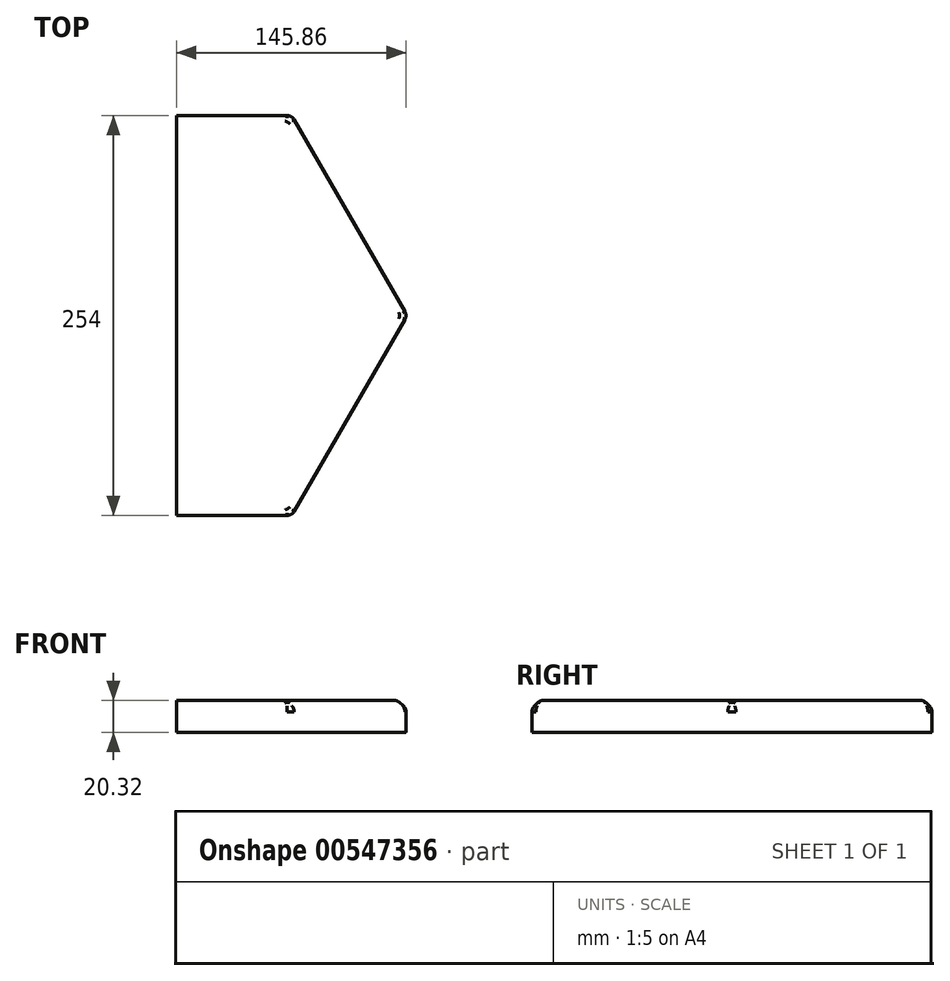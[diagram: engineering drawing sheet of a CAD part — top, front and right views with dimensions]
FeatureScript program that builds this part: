
annotation { "Feature Type Name" : "Feature", "Feature Type Description" : "" }
export const myFeature = defineFeature(function(context is Context, id is Id, definition is map)
    precondition{}
    {
        {
            var Q0;
            Q0=qCreatedBy(makeId("Top.planeOp"),FACE);
            var sketch = newSketch(context, id + "F0", { "sketchPlane" : qUnion([Q0])});
            skCircle(sketch, "E0.cCircle", {"center": v(0, 0) * mm, "radius": 127 * mm, "construction": true});
            skLineSegment(sketch, "E0.0", {"start": v(73.32, 127) * mm, "end": v(146.65, 0) * mm});
            skLineSegment(sketch, "E0.1", {"start": v(146.65, 0) * mm, "end": v(73.32, -127) * mm});
            skLineSegment(sketch, "E0.2", {"start": v(73.32, -127) * mm, "end": v(-73.32, -127) * mm});
            skLineSegment(sketch, "E0.3", {"start": v(-73.32, -127) * mm, "end": v(-146.65, 0) * mm});
            skLineSegment(sketch, "E0.4", {"start": v(-146.65, 0) * mm, "end": v(-73.32, 127) * mm});
            skLineSegment(sketch, "E0.5", {"start": v(-73.32, 127) * mm, "end": v(73.32, 127) * mm});
            skPoint(sketch, "E0.0.midPoint", {"position": v(109.99, 63.5) * mm});
            skSolve(sketch);
        }
        {
            var Q0;
            Q0 = qSketchRegion(id + "F0", true);
            extrude(context, id + "F1", {"entities" : qUnion([Q0]), "depth" : 20.32 * mm, "offsetDistance" : 25.4 * mm});
        }
        {
            var Q0;
            Q0=makeQuery(id+"F1.opExtrude","CAP_EDGE",EDGE,{"disambiguationData":[OSD([sQuery(id+"F0.wireOp",EDGE,"E0.3")])],"isStart":false});
            var Q1;
            Q1=makeQuery(id+"F1.opExtrude","CAP_EDGE",EDGE,{"disambiguationData":[OSD([sQuery(id+"F0.wireOp",EDGE,"E0.2")])],"isStart":false});
            var Q2;
            Q2=makeQuery(id+"F1.opExtrude","CAP_EDGE",EDGE,{"disambiguationData":[OSD([sQuery(id+"F0.wireOp",EDGE,"E0.1")])],"isStart":false});
            var Q3;
            Q3=makeQuery(id+"F1.opExtrude","CAP_EDGE",EDGE,{"disambiguationData":[OSD([sQuery(id+"F0.wireOp",EDGE,"E0.0")])],"isStart":false});
            var Q4;
            Q4=makeQuery(id+"F1.opExtrude","CAP_EDGE",EDGE,{"disambiguationData":[OSD([sQuery(id+"F0.wireOp",EDGE,"E0.5")])],"isStart":false});
            var Q5;
            Q5=makeQuery(id+"F1.opExtrude","CAP_EDGE",EDGE,{"disambiguationData":[OSD([sQuery(id+"F0.wireOp",EDGE,"E0.4")])],"isStart":false});
            chamfer(context, id + "F2", {"entities" : qUnion([Q0, Q1, Q2, Q3, Q4, Q5]), "width" : 5.08 * mm, "tangentPropagation" : true});
        }
        {
            var Q0;
            Q0=makeQuery(id+"F1.opExtrude","CAP_FACE",FACE,{"disambiguationData":[OSD([sQuery(id+"F0.wireOp",EDGE,"E0.0"),sQuery(id+"F0.wireOp",EDGE,"E0.1"),sQuery(id+"F0.wireOp",EDGE,"E0.2"),sQuery(id+"F0.wireOp",EDGE,"E0.3"),sQuery(id+"F0.wireOp",EDGE,"E0.4"),sQuery(id+"F0.wireOp",EDGE,"E0.5")])],"isStart":false});
            var sketch = newSketch(context, id + "F3", { "sketchPlane" : qUnion([Q0])});
            skLineSegment(sketch, "E1.bottom", {"start": v(0, 161.52) * mm, "end": v(-159.86, 161.52) * mm});
            skLineSegment(sketch, "E1.top", {"start": v(0, -144.8) * mm, "end": v(-159.86, -144.8) * mm});
            skLineSegment(sketch, "E1.left", {"start": v(0, 161.52) * mm, "end": v(0, -144.8) * mm});
            skLineSegment(sketch, "E1.right", {"start": v(-159.86, 161.52) * mm, "end": v(-159.86, -144.8) * mm});
            skSolve(sketch);
        }
        {
            var Q0;
            {var subQ9=sQuery(id+"F3.wireOp",EDGE,"E1.bottom");Q0=makeQuery(id+"F3.imprint","IMPRINT",FACE,{"disambiguationData":[TD([[makeQuery(id+"F3.imprint","IMPRINT",EDGE,{"derivedFrom":subQ9}),1.0]])]});}
            var Q1;
            {var subQ0=sQuery(id+"F0.wireOp",EDGE,"E0.5");var subQ1=sQuery(id+"F0.wireOp",EDGE,"E0.4");var subQ2=sQuery(id+"F0.wireOp",EDGE,"E0.3");var subQ3=sQuery(id+"F0.wireOp",EDGE,"E0.2");var subQ4=makeQuery(id+"F1.opExtrude","CAP_FACE",FACE,{"disambiguationData":[OSD([sQuery(id+"F0.wireOp",EDGE,"E0.0"),sQuery(id+"F0.wireOp",EDGE,"E0.1"),subQ3,subQ2,subQ1,subQ0])],"isStart":false});var subQ5=makeQuery(id+"F2.opChamfer","BLEND_EDGE",EDGE,{"blendedFrom":[makeQuery(id+"F1.opExtrude","CAP_EDGE",EDGE,{"disambiguationData":[OSD([subQ2])],"isStart":false}),subQ4],"blendedInto":[subQ4]});Q1=makeQuery(id+"F3.imprint","IMPRINT",FACE,{"disambiguationData":[TD([[makeQuery(id+"F3.imprint","IMPRINT",EDGE,{"derivedFrom":subQ5}),1.0]])]});}
            extrude(context, id + "F4", {"entities" : qUnion([Q0, Q1]), "operationType" : NewBodyOperationType.REMOVE, "endBound" : BoundingType.THROUGH_ALL, "oppositeDirection" : true, "depth" : 25.4 * mm, "offsetDistance" : 25.4 * mm});
        }
        {
            var Q0;
            {var subQ0=sQuery(id+"F0.wireOp",EDGE,"E0.2");Q0=makeQuery(id+"F2.opChamfer","BLEND_EDGE",EDGE,{"blendedFrom":[makeQuery(id+"F1.opExtrude","CAP_EDGE",EDGE,{"disambiguationData":[OSD([subQ0])],"isStart":false}),makeQuery(id+"F1.opExtrude","CAP_FACE",FACE,{"disambiguationData":[OSD([sQuery(id+"F0.wireOp",EDGE,"E0.0"),sQuery(id+"F0.wireOp",EDGE,"E0.1"),subQ0,sQuery(id+"F0.wireOp",EDGE,"E0.3"),sQuery(id+"F0.wireOp",EDGE,"E0.4"),sQuery(id+"F0.wireOp",EDGE,"E0.5")])],"isStart":false})],"blendedInto":[makeQuery(id+"F1.opExtrude","CAP_FACE",FACE,{"disambiguationData":[OSD([sQuery(id+"F0.wireOp",EDGE,"E0.0"),sQuery(id+"F0.wireOp",EDGE,"E0.1"),subQ0,sQuery(id+"F0.wireOp",EDGE,"E0.3"),sQuery(id+"F0.wireOp",EDGE,"E0.4"),sQuery(id+"F0.wireOp",EDGE,"E0.5")])],"isStart":false})]});}
            var Q1;
            {var subQ0=sQuery(id+"F0.wireOp",EDGE,"E0.1");Q1=makeQuery(id+"F2.opChamfer","BLEND_EDGE",EDGE,{"blendedFrom":[makeQuery(id+"F1.opExtrude","CAP_EDGE",EDGE,{"disambiguationData":[OSD([subQ0])],"isStart":false}),makeQuery(id+"F1.opExtrude","CAP_FACE",FACE,{"disambiguationData":[OSD([sQuery(id+"F0.wireOp",EDGE,"E0.0"),subQ0,sQuery(id+"F0.wireOp",EDGE,"E0.2"),sQuery(id+"F0.wireOp",EDGE,"E0.3"),sQuery(id+"F0.wireOp",EDGE,"E0.4"),sQuery(id+"F0.wireOp",EDGE,"E0.5")])],"isStart":false})],"blendedInto":[makeQuery(id+"F1.opExtrude","CAP_FACE",FACE,{"disambiguationData":[OSD([sQuery(id+"F0.wireOp",EDGE,"E0.0"),subQ0,sQuery(id+"F0.wireOp",EDGE,"E0.2"),sQuery(id+"F0.wireOp",EDGE,"E0.3"),sQuery(id+"F0.wireOp",EDGE,"E0.4"),sQuery(id+"F0.wireOp",EDGE,"E0.5")])],"isStart":false})]});}
            var Q2;
            {var subQ0=sQuery(id+"F0.wireOp",EDGE,"E0.0");Q2=makeQuery(id+"F2.opChamfer","BLEND_EDGE",EDGE,{"blendedFrom":[makeQuery(id+"F1.opExtrude","CAP_EDGE",EDGE,{"disambiguationData":[OSD([subQ0])],"isStart":false}),makeQuery(id+"F1.opExtrude","CAP_FACE",FACE,{"disambiguationData":[OSD([subQ0,sQuery(id+"F0.wireOp",EDGE,"E0.1"),sQuery(id+"F0.wireOp",EDGE,"E0.2"),sQuery(id+"F0.wireOp",EDGE,"E0.3"),sQuery(id+"F0.wireOp",EDGE,"E0.4"),sQuery(id+"F0.wireOp",EDGE,"E0.5")])],"isStart":false})],"blendedInto":[makeQuery(id+"F1.opExtrude","CAP_FACE",FACE,{"disambiguationData":[OSD([subQ0,sQuery(id+"F0.wireOp",EDGE,"E0.1"),sQuery(id+"F0.wireOp",EDGE,"E0.2"),sQuery(id+"F0.wireOp",EDGE,"E0.3"),sQuery(id+"F0.wireOp",EDGE,"E0.4"),sQuery(id+"F0.wireOp",EDGE,"E0.5")])],"isStart":false})]});}
            var Q3;
            {var subQ0=sQuery(id+"F0.wireOp",EDGE,"E0.5");Q3=makeQuery(id+"F2.opChamfer","BLEND_EDGE",EDGE,{"blendedFrom":[makeQuery(id+"F1.opExtrude","CAP_EDGE",EDGE,{"disambiguationData":[OSD([subQ0])],"isStart":false}),makeQuery(id+"F1.opExtrude","CAP_FACE",FACE,{"disambiguationData":[OSD([sQuery(id+"F0.wireOp",EDGE,"E0.0"),sQuery(id+"F0.wireOp",EDGE,"E0.1"),sQuery(id+"F0.wireOp",EDGE,"E0.2"),sQuery(id+"F0.wireOp",EDGE,"E0.3"),sQuery(id+"F0.wireOp",EDGE,"E0.4"),subQ0])],"isStart":false})],"blendedInto":[makeQuery(id+"F1.opExtrude","CAP_FACE",FACE,{"disambiguationData":[OSD([sQuery(id+"F0.wireOp",EDGE,"E0.0"),sQuery(id+"F0.wireOp",EDGE,"E0.1"),sQuery(id+"F0.wireOp",EDGE,"E0.2"),sQuery(id+"F0.wireOp",EDGE,"E0.3"),sQuery(id+"F0.wireOp",EDGE,"E0.4"),subQ0])],"isStart":false})]});}
            var Q4;
            {var subQ0=sQuery(id+"F0.wireOp",EDGE,"E0.2");Q4=makeQuery(id+"F2.opChamfer","BLEND_EDGE",EDGE,{"blendedFrom":[makeQuery(id+"F1.opExtrude","CAP_EDGE",EDGE,{"disambiguationData":[OSD([subQ0])],"isStart":false}),makeQuery(id+"F1.opExtrude","SWEPT_FACE",FACE,{"disambiguationData":[OSD([subQ0])]})],"blendedInto":[makeQuery(id+"F1.opExtrude","SWEPT_FACE",FACE,{"disambiguationData":[OSD([subQ0])]})]});}
            var Q5;
            {var subQ0=sQuery(id+"F0.wireOp",EDGE,"E0.1");Q5=makeQuery(id+"F2.opChamfer","BLEND_EDGE",EDGE,{"blendedFrom":[makeQuery(id+"F1.opExtrude","CAP_EDGE",EDGE,{"disambiguationData":[OSD([subQ0])],"isStart":false}),makeQuery(id+"F1.opExtrude","SWEPT_FACE",FACE,{"disambiguationData":[OSD([subQ0])]})],"blendedInto":[makeQuery(id+"F1.opExtrude","SWEPT_FACE",FACE,{"disambiguationData":[OSD([subQ0])]})]});}
            var Q6;
            Q6=makeQuery(id+"F1.opExtrude","SWEPT_EDGE",EDGE,{"disambiguationData":[OSD([sQuery(id+"F0.wireOp",EDGE,"E0.1"),sQuery(id+"F0.wireOp",EDGE,"E0.2")])]});
            var Q7;
            Q7=makeQuery(id+"F2.opChamfer","BLEND_EDGE",EDGE,{"blendedFrom":[makeQuery(id+"F1.opExtrude","CAP_EDGE",EDGE,{"disambiguationData":[OSD([sQuery(id+"F0.wireOp",EDGE,"E0.1")])],"isStart":false}),makeQuery(id+"F1.opExtrude","CAP_EDGE",EDGE,{"disambiguationData":[OSD([sQuery(id+"F0.wireOp",EDGE,"E0.2")])],"isStart":false})],"blendedInto":[]});
            var Q8;
            Q8=makeQuery(id+"F2.opChamfer","BLEND_EDGE",EDGE,{"blendedFrom":[makeQuery(id+"F1.opExtrude","CAP_EDGE",EDGE,{"disambiguationData":[OSD([sQuery(id+"F0.wireOp",EDGE,"E0.0")])],"isStart":false}),makeQuery(id+"F1.opExtrude","CAP_EDGE",EDGE,{"disambiguationData":[OSD([sQuery(id+"F0.wireOp",EDGE,"E0.1")])],"isStart":false})],"blendedInto":[]});
            var Q9;
            Q9=makeQuery(id+"F1.opExtrude","SWEPT_EDGE",EDGE,{"disambiguationData":[OSD([sQuery(id+"F0.wireOp",EDGE,"E0.0"),sQuery(id+"F0.wireOp",EDGE,"E0.1")])]});
            var Q10;
            {var subQ0=sQuery(id+"F0.wireOp",EDGE,"E0.0");Q10=makeQuery(id+"F2.opChamfer","BLEND_EDGE",EDGE,{"blendedFrom":[makeQuery(id+"F1.opExtrude","CAP_EDGE",EDGE,{"disambiguationData":[OSD([subQ0])],"isStart":false}),makeQuery(id+"F1.opExtrude","SWEPT_FACE",FACE,{"disambiguationData":[OSD([subQ0])]})],"blendedInto":[makeQuery(id+"F1.opExtrude","SWEPT_FACE",FACE,{"disambiguationData":[OSD([subQ0])]})]});}
            var Q11;
            Q11=makeQuery(id+"F2.opChamfer","BLEND_EDGE",EDGE,{"blendedFrom":[makeQuery(id+"F1.opExtrude","CAP_EDGE",EDGE,{"disambiguationData":[OSD([sQuery(id+"F0.wireOp",EDGE,"E0.0")])],"isStart":false}),makeQuery(id+"F1.opExtrude","CAP_EDGE",EDGE,{"disambiguationData":[OSD([sQuery(id+"F0.wireOp",EDGE,"E0.5")])],"isStart":false})],"blendedInto":[]});
            var Q12;
            Q12=makeQuery(id+"F1.opExtrude","SWEPT_EDGE",EDGE,{"disambiguationData":[OSD([sQuery(id+"F0.wireOp",EDGE,"E0.0"),sQuery(id+"F0.wireOp",EDGE,"E0.5")])]});
            var Q13;
            {var subQ0=sQuery(id+"F0.wireOp",EDGE,"E0.5");Q13=makeQuery(id+"F2.opChamfer","BLEND_EDGE",EDGE,{"blendedFrom":[makeQuery(id+"F1.opExtrude","CAP_EDGE",EDGE,{"disambiguationData":[OSD([subQ0])],"isStart":false}),makeQuery(id+"F1.opExtrude","SWEPT_FACE",FACE,{"disambiguationData":[OSD([subQ0])]})],"blendedInto":[makeQuery(id+"F1.opExtrude","SWEPT_FACE",FACE,{"disambiguationData":[OSD([subQ0])]})]});}
            fillet(context, id + "F5", {"entities" : qUnion([Q0, Q1, Q2, Q3, Q4, Q5, Q6, Q7, Q8, Q9, Q10, Q11, Q12, Q13]), "radius" : 5.08 * mm, "tangentPropagation" : true, "allowEdgeOverflow" : false});
        }
    });
